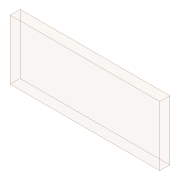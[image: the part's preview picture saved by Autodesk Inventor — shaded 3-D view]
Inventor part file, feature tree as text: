
AUTODESK INVENTOR PART (.ipt)
format: ipt  version: 2020 (Build 240168000, 168)  size: 81,408 bytes
history: native  units: mm
features: extrude x1, sketch x1
ambient origin geometry x8: Origin, YZ Plane, XZ Plane, XY Plane, X Axis, Y Axis, Z Axis, Center Point
bodies: Solid1 (feature_tree)
feature tree (2):
  extrude  "Extrusion1"  Depth=30.0mm
  sketch  "Sketch1"  dims[d0=75.0mm d1=30.0mm d2=5.0mm d3=0.0mm]
